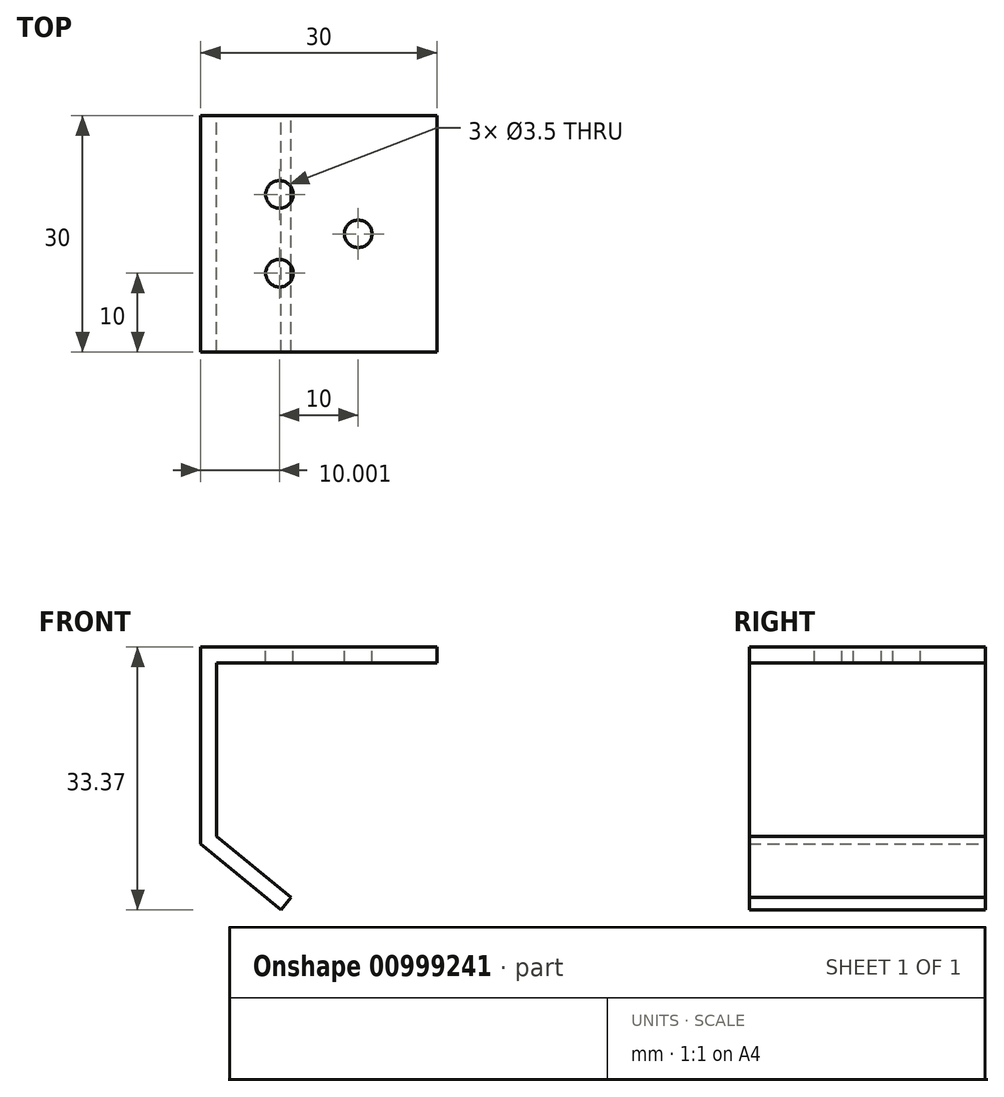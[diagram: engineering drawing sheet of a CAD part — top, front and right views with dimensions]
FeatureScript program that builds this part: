
annotation { "Feature Type Name" : "Feature", "Feature Type Description" : "" }
export const myFeature = defineFeature(function(context is Context, id is Id, definition is map)
    precondition{}
    {
        {
            var Q0;
            Q0=qCreatedBy(makeId("Front.planeOp"),FACE);
            var sketch = newSketch(context, id + "F0", { "sketchPlane" : qUnion([Q0])});
            skLineSegment(sketch, "E0", {"start": v(-2.96, 7.36) * mm, "end": v(27.04, 7.36) * mm});
            skLineSegment(sketch, "E1", {"start": v(27.04, 7.36) * mm, "end": v(27.04, 5.36) * mm});
            skLineSegment(sketch, "E2", {"start": v(27.04, 5.36) * mm, "end": v(-0.96, 5.36) * mm});
            skLineSegment(sketch, "E3", {"start": v(-0.96, 5.36) * mm, "end": v(-0.96, -16.69) * mm});
            skLineSegment(sketch, "E4", {"start": v(-0.96, -16.69) * mm, "end": v(8.5, -24.46) * mm});
            skLineSegment(sketch, "E5", {"start": v(8.5, -24.46) * mm, "end": v(7.23, -26) * mm});
            skLineSegment(sketch, "E6", {"start": v(7.23, -26) * mm, "end": v(-2.96, -17.64) * mm});
            skLineSegment(sketch, "E7", {"start": v(-2.96, -17.64) * mm, "end": v(-2.96, 7.36) * mm});
            skSolve(sketch);
        }
        {
            var Q0;
            Q0=qSketchRegion(id+"F0",true);
            extrude(context, id + "F1", {"entities" : qUnion([Q0]), "depth" : 30 * mm, "offsetDistance" : 25 * mm});
        }
        {
            var Q0;
            Q0=makeQuery(id+"F1.opExtrude","SWEPT_FACE",FACE,{"disambiguationData":[OSD([sQuery(id+"F0.wireOp",EDGE,"E0")])]});
            var sketch = newSketch(context, id + "F2", { "sketchPlane" : qUnion([Q0])});
            skPoint(sketch, "E8", {"position": v(7.04, -10) * mm});
            skPoint(sketch, "E9", {"position": v(7.04, -20) * mm});
            skPoint(sketch, "E10", {"position": v(17.04, -15) * mm});
            skSolve(sketch);
        }
        {
            var Q0;
            Q0=sQuery(id+"F2.wireOp",VERTEX,"E8");
            var Q1;
            Q1=sQuery(id+"F2.wireOp",VERTEX,"E10");
            var Q2;
            Q2=sQuery(id+"F2.wireOp",VERTEX,"E9");
            var Q3;
            Q3=makeQuery(id+"F1.opExtrude","SWEPT_BODY",BODY,{"disambiguationData":[OSD([sQuery(id+"F0.wireOp",EDGE,"E0"),sQuery(id+"F0.wireOp",EDGE,"E1"),sQuery(id+"F0.wireOp",EDGE,"E2"),sQuery(id+"F0.wireOp",EDGE,"E3"),sQuery(id+"F0.wireOp",EDGE,"E4"),sQuery(id+"F0.wireOp",EDGE,"E5"),sQuery(id+"F0.wireOp",EDGE,"E6"),sQuery(id+"F0.wireOp",EDGE,"E7")])]});
            hole(context, id + "F3", {"style" : HoleStyle.SIMPLE, "endStyle" : HoleEndStyle.BLIND, "holeDiameter" : 3.5 * mm, "majorDiameter" : 5 * mm, "holeDepth" : 5 * mm, "isTappedThrough" : true, "tappedDepth" : 12 * mm, "tapClearance" : 3, "locations" : qUnion([Q0, Q1, Q2]), "scope" : qUnion([Q3])});
        }
    });
